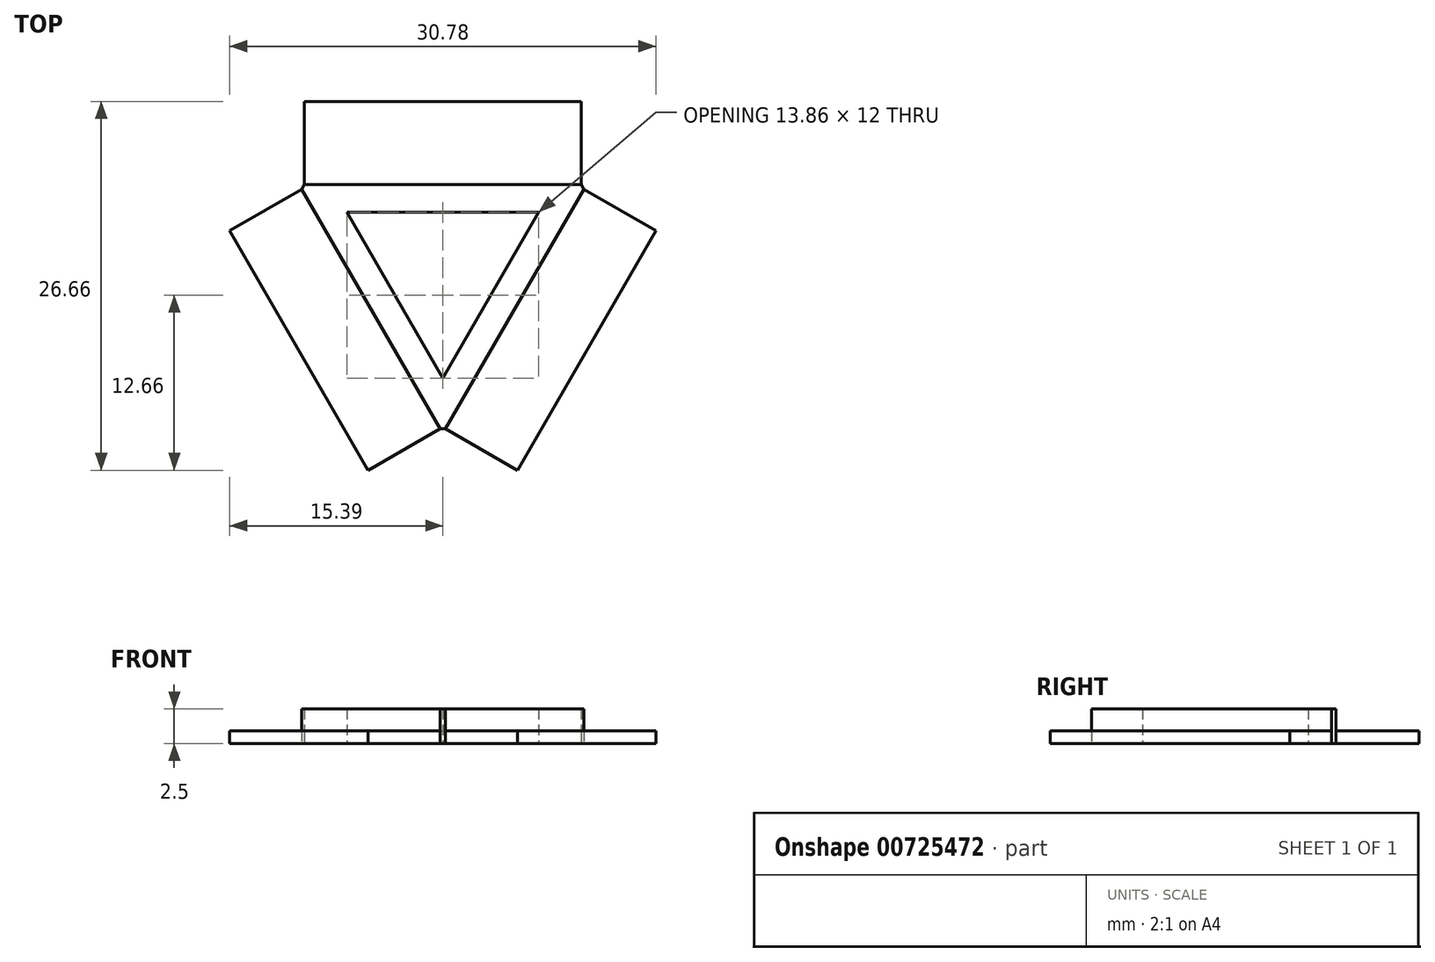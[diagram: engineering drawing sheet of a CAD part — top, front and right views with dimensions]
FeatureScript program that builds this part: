
annotation { "Feature Type Name" : "Feature", "Feature Type Description" : "" }
export const myFeature = defineFeature(function(context is Context, id is Id, definition is map)
    precondition{}
    {
        {
            var Q0;
            Q0=qCreatedBy(makeId("Top.planeOp"),FACE);
            var sketch = newSketch(context, id + "F0", { "sketchPlane" : qUnion([Q0])});
            skCircle(sketch, "E0", {"center": v(0, 0) * mm, "radius": 6 * mm, "construction": true});
            skCircle(sketch, "E1", {"center": v(0, 0) * mm, "radius": 4 * mm, "construction": true});
            skLineSegment(sketch, "E2.bottom", {"start": v(-10, 12) * mm, "end": v(10, 12) * mm});
            skLineSegment(sketch, "E2.top", {"start": v(-10, 6) * mm, "end": v(10, 6) * mm});
            skLineSegment(sketch, "E2.left", {"start": v(-10, 12) * mm, "end": v(-10, 6) * mm});
            skLineSegment(sketch, "E2.right", {"start": v(10, 12) * mm, "end": v(10, 6) * mm});
            skPoint(sketch, "E3", {"position": v(0, 6) * mm});
            skLineSegment(sketch, "E4.1.0", {"start": v(-0.2, -11.66) * mm, "end": v(-10.2, 5.66) * mm});
            skLineSegment(sketch, "E4.1.1", {"start": v(-5.4, -14.66) * mm, "end": v(-0.2, -11.66) * mm});
            skLineSegment(sketch, "E4.1.2", {"start": v(-5.4, -14.66) * mm, "end": v(-15.4, 2.66) * mm});
            skLineSegment(sketch, "E4.1.3", {"start": v(-15.4, 2.66) * mm, "end": v(-10.2, 5.66) * mm});
            skLineSegment(sketch, "E4.2.0", {"start": v(10.2, 5.66) * mm, "end": v(0.2, -11.66) * mm});
            skLineSegment(sketch, "E4.2.1", {"start": v(15.4, 2.66) * mm, "end": v(10.2, 5.66) * mm});
            skLineSegment(sketch, "E4.2.2", {"start": v(15.4, 2.66) * mm, "end": v(5.4, -14.66) * mm});
            skLineSegment(sketch, "E4.2.3", {"start": v(5.4, -14.66) * mm, "end": v(0.2, -11.66) * mm});
            skLineSegment(sketch, "E5", {"start": v(-10.2, 5.66) * mm, "end": v(-10, 6) * mm});
            skLineSegment(sketch, "E6", {"start": v(-0.2, -11.66) * mm, "end": v(0.2, -11.66) * mm});
            skLineSegment(sketch, "E7", {"start": v(10, 6) * mm, "end": v(10.2, 5.66) * mm});
            skLineSegment(sketch, "E8.0", {"start": v(0, -8) * mm, "end": v(-6.93, 4) * mm});
            skLineSegment(sketch, "E8.1", {"start": v(-6.93, 4) * mm, "end": v(6.93, 4) * mm});
            skLineSegment(sketch, "E8.2", {"start": v(6.93, 4) * mm, "end": v(0, -8) * mm});
            skPoint(sketch, "E8.0.midPoint", {"position": v(-3.46, -2) * mm});
            skSolve(sketch);
        }
        {
            var Q0;
            Q0=makeQuery(id+"F0.imprint","IMPRINT",FACE,{"disambiguationData":[TD([[makeQuery(id+"F0.imprint","IMPRINT",EDGE,{"derivedFrom":sQuery(id+"F0.wireOp",EDGE,"E4.1.0")}),1.0]])]});
            var Q1;
            Q1=makeQuery(id+"F0.imprint","IMPRINT",FACE,{"disambiguationData":[TD([[makeQuery(id+"F0.imprint","IMPRINT",EDGE,{"derivedFrom":sQuery(id+"F0.wireOp",EDGE,"E2.bottom")}),-1.0]])]});
            var Q2;
            Q2=makeQuery(id+"F0.imprint","IMPRINT",FACE,{"disambiguationData":[TD([[makeQuery(id+"F0.imprint","IMPRINT",EDGE,{"derivedFrom":sQuery(id+"F0.wireOp",EDGE,"E4.2.0")}),1.0]])]});
            extrude(context, id + "F1", {"entities" : qUnion([Q0, Q1, Q2]), "depth" : 0.9 * mm, "offsetDistance" : 25 * mm});
        }
        {
            var Q0;
            Q0=makeQuery(id+"F0.imprint","IMPRINT",FACE,{"disambiguationData":[TD([[makeQuery(id+"F0.imprint","IMPRINT",EDGE,{"derivedFrom":sQuery(id+"F0.wireOp",EDGE,"E2.top")}),-1.0]])]});
            extrude(context, id + "F2", {"entities" : qUnion([Q0]), "depth" : 2.5 * mm, "offsetDistance" : 25 * mm});
        }
    });
